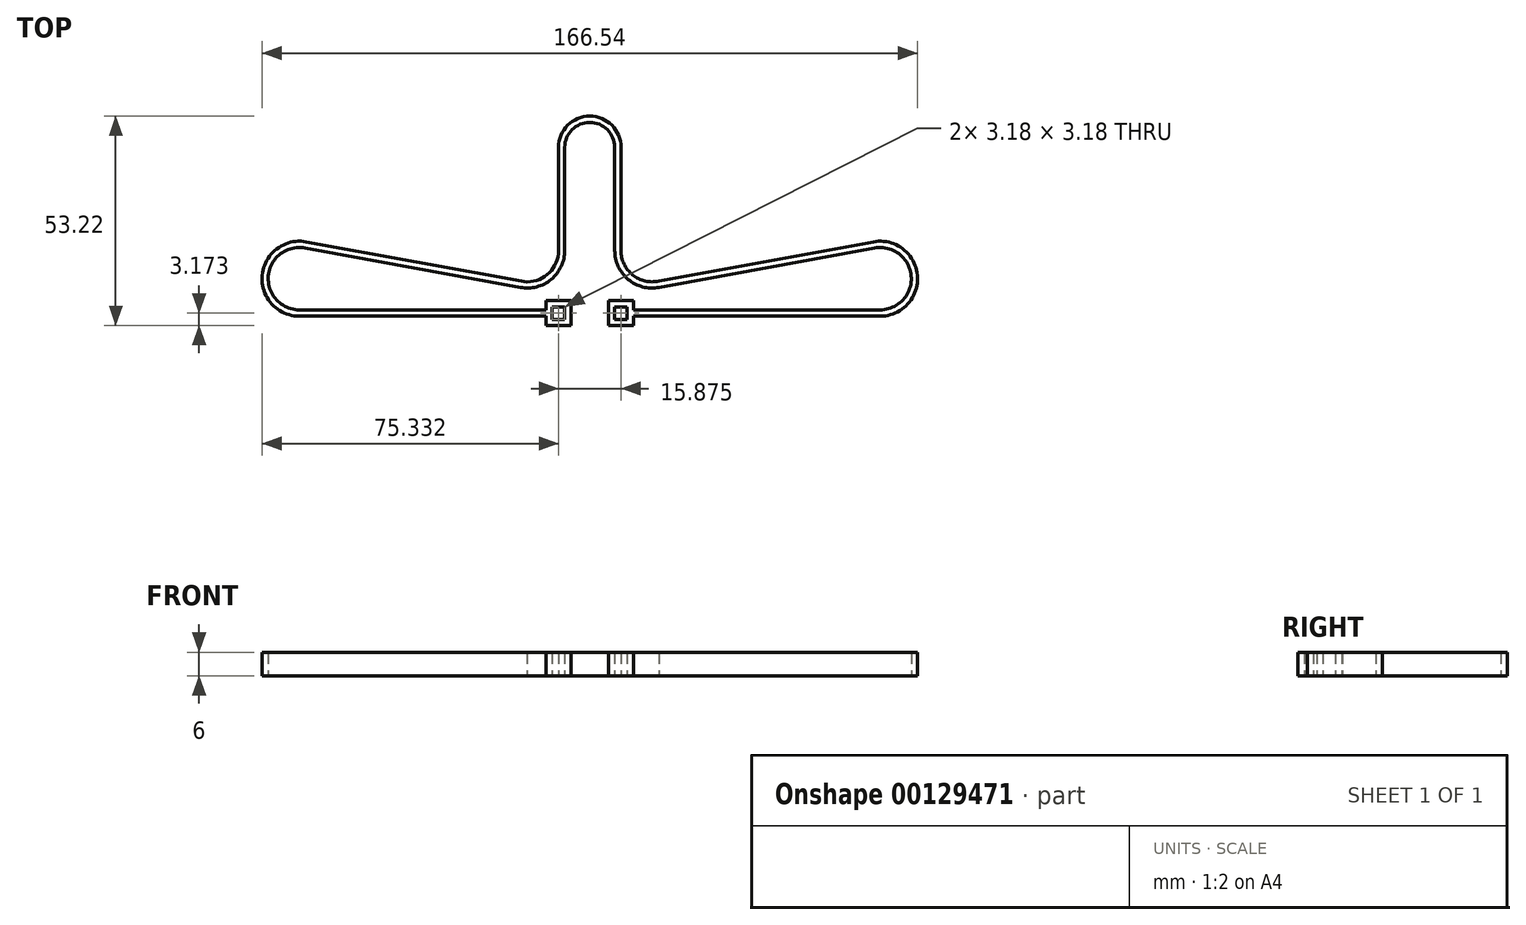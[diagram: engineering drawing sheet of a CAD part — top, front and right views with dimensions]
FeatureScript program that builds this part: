
annotation { "Feature Type Name" : "Feature", "Feature Type Description" : "" }
export const myFeature = defineFeature(function(context is Context, id is Id, definition is map)
    precondition{}
    {
        {
            var Q0;
            Q0=qCreatedBy(makeId("Top.planeOp"),FACE);
            var sketch = newSketch(context, id + "F0", { "sketchPlane" : qUnion([Q0])});
            skLineSegment(sketch, "E0", {"start": v(0, 0) * mm, "end": v(0, -26.23) * mm, "construction": true});
            skLineSegment(sketch, "E1", {"start": v(-15.88, -26.23) * mm, "end": v(15.88, -26.23) * mm, "construction": true});
            skCircle(sketch, "E2", {"center": v(0, 0) * mm, "radius": 6.35 * mm, "construction": true});
            skCircle(sketch, "E3", {"center": v(-15.88, -26.23) * mm, "radius": 7.94 * mm, "construction": true});
            skCircle(sketch, "E4", {"center": v(15.88, -26.23) * mm, "radius": 7.94 * mm, "construction": true});
            skLineSegment(sketch, "E5", {"start": v(0, -26.23) * mm, "end": v(0, -33.38) * mm, "construction": true});
            skLineSegment(sketch, "E6", {"start": v(-73.75, -33.38) * mm, "end": v(73.75, -33.38) * mm, "construction": true});
            skCircle(sketch, "E7", {"center": v(73.75, -33.38) * mm, "radius": 7.94 * mm, "construction": true});
            skCircle(sketch, "E8", {"center": v(-73.75, -33.38) * mm, "radius": 7.94 * mm, "construction": true});
            skLineSegment(sketch, "E9", {"start": v(-6.35, 0) * mm, "end": v(-6.35, -26.23) * mm});
            skLineSegment(sketch, "E10", {"start": v(-17.6, -35.6) * mm, "end": v(-72.32, -25.57) * mm});
            skLineSegment(sketch, "E11", {"start": v(6.35, -26.23) * mm, "end": v(6.35, 0) * mm});
            skArc(sketch, "E12", {"start": v(-17.6, -35.6) * mm, "mid": v(-9.78, -33.55) * mm, "end": v(-6.35, -26.23) * mm});
            skArc(sketch, "E13", {"start": v(6.35, -26.23) * mm, "mid": v(9.78, -33.55) * mm, "end": v(17.6, -35.6) * mm});
            skLineSegment(sketch, "E14", {"start": v(17.6, -35.6) * mm, "end": v(72.32, -25.57) * mm});
            skArc(sketch, "E15", {"start": v(6.35, 0) * mm, "mid": v(0, 6.35) * mm, "end": v(-6.35, 0) * mm});
            skArc(sketch, "E16", {"start": v(73.75, -41.31) * mm, "mid": v(81.65, -32.66) * mm, "end": v(72.32, -25.57) * mm});
            skArc(sketch, "E17", {"start": v(-72.32, -25.57) * mm, "mid": v(-81.65, -32.66) * mm, "end": v(-73.75, -41.31) * mm});
            skArc(sketch, "E18", {"start": v(-15.88, -34.17) * mm, "mid": v(-10.26, -31.84) * mm, "end": v(-7.94, -26.23) * mm});
            skArc(sketch, "E19", {"start": v(7.94, -26.23) * mm, "mid": v(10.9, -32.42) * mm, "end": v(17.6, -33.98) * mm});
            skLineSegment(sketch, "E20", {"start": v(-6.35, 0) * mm, "end": v(-7.94, 0) * mm, "construction": true});
            skLineSegment(sketch, "E21", {"start": v(6.35, 0) * mm, "end": v(7.94, 0) * mm, "construction": true});
            skLineSegment(sketch, "E22", {"start": v(-7.94, 0) * mm, "end": v(-7.94, -26.23) * mm});
            skLineSegment(sketch, "E23", {"start": v(7.94, 0) * mm, "end": v(7.94, -26.23) * mm});
            skArc(sketch, "E24", {"start": v(7.94, 0) * mm, "mid": v(0, 7.94) * mm, "end": v(-7.94, 0) * mm});
            skLineSegment(sketch, "E25", {"start": v(-15.88, -34.17) * mm, "end": v(-72.05, -24) * mm});
            skLineSegment(sketch, "E26", {"start": v(17.6, -33.98) * mm, "end": v(72.03, -24) * mm});
            skArc(sketch, "E27", {"start": v(73.75, -42.9) * mm, "mid": v(83.23, -32.51) * mm, "end": v(72.03, -24) * mm});
            skArc(sketch, "E28", {"start": v(-72.05, -24) * mm, "mid": v(-83.23, -32.52) * mm, "end": v(-73.75, -42.9) * mm});
            skLineSegment(sketch, "E29", {"start": v(-73.75, -41.31) * mm, "end": v(-11.11, -41.31) * mm});
            skLineSegment(sketch, "E30", {"start": v(-73.75, -42.9) * mm, "end": v(-11.11, -42.9) * mm});
            skLineSegment(sketch, "E31", {"start": v(73.75, -41.31) * mm, "end": v(11.11, -41.31) * mm});
            skLineSegment(sketch, "E32", {"start": v(73.75, -42.9) * mm, "end": v(11.11, -42.9) * mm});
            skLineSegment(sketch, "E33", {"start": v(-11.11, -42.9) * mm, "end": v(-11.11, -41.31) * mm});
            skLineSegment(sketch, "E34", {"start": v(-11.11, -41.31) * mm, "end": v(-11.11, -38.93) * mm});
            skLineSegment(sketch, "E35", {"start": v(-11.11, -38.93) * mm, "end": v(-4.76, -38.93) * mm});
            skLineSegment(sketch, "E36", {"start": v(-4.76, -38.93) * mm, "end": v(-4.76, -45.28) * mm});
            skLineSegment(sketch, "E37", {"start": v(-4.76, -45.28) * mm, "end": v(-11.11, -45.28) * mm});
            skLineSegment(sketch, "E38", {"start": v(-11.11, -45.28) * mm, "end": v(-11.11, -42.9) * mm});
            skLineSegment(sketch, "E39", {"start": v(-11.11, -42.1) * mm, "end": v(-4.76, -42.1) * mm, "construction": true});
            skLineSegment(sketch, "E40.rect.bottom", {"start": v(-6.35, -40.52) * mm, "end": v(-9.52, -40.52) * mm});
            skLineSegment(sketch, "E40.rect.top", {"start": v(-6.35, -43.7) * mm, "end": v(-9.52, -43.7) * mm});
            skLineSegment(sketch, "E40.rect.left", {"start": v(-6.35, -40.52) * mm, "end": v(-6.35, -43.7) * mm});
            skLineSegment(sketch, "E40.rect.right", {"start": v(-9.52, -40.52) * mm, "end": v(-9.52, -43.7) * mm});
            skPoint(sketch, "E40.rect.middle", {"position": v(-7.94, -42.1) * mm});
            skLineSegment(sketch, "E41", {"start": v(-9.52, -40.52) * mm, "end": v(-11.11, -40.52) * mm, "construction": true});
            skLineSegment(sketch, "E42", {"start": v(-9.52, -40.52) * mm, "end": v(-9.52, -38.93) * mm, "construction": true});
            skLineSegment(sketch, "E43", {"start": v(11.11, -42.9) * mm, "end": v(11.11, -41.31) * mm});
            skLineSegment(sketch, "E44", {"start": v(0, -33.38) * mm, "end": v(0, -42.1) * mm, "construction": true});
            skLineSegment(sketch, "E45", {"start": v(11.11, -41.31) * mm, "end": v(11.11, -38.93) * mm});
            skLineSegment(sketch, "E46", {"start": v(11.11, -38.93) * mm, "end": v(4.76, -38.93) * mm});
            skLineSegment(sketch, "E47", {"start": v(4.76, -38.93) * mm, "end": v(4.76, -45.28) * mm});
            skLineSegment(sketch, "E48", {"start": v(4.76, -45.28) * mm, "end": v(11.11, -45.28) * mm});
            skLineSegment(sketch, "E49", {"start": v(11.11, -45.28) * mm, "end": v(11.11, -42.9) * mm});
            skLineSegment(sketch, "E50", {"start": v(4.76, -42.1) * mm, "end": v(11.11, -42.1) * mm, "construction": true});
            skLineSegment(sketch, "E51.rect.bottom", {"start": v(6.35, -40.52) * mm, "end": v(9.53, -40.52) * mm});
            skLineSegment(sketch, "E51.rect.top", {"start": v(6.35, -43.7) * mm, "end": v(9.53, -43.7) * mm});
            skLineSegment(sketch, "E51.rect.left", {"start": v(6.35, -40.52) * mm, "end": v(6.35, -43.7) * mm});
            skLineSegment(sketch, "E51.rect.right", {"start": v(9.53, -40.52) * mm, "end": v(9.53, -43.7) * mm});
            skPoint(sketch, "E51.rect.middle", {"position": v(7.94, -42.1) * mm});
            skLineSegment(sketch, "E52", {"start": v(-4.76, -42.1) * mm, "end": v(4.76, -42.1) * mm, "construction": true});
            skLineSegment(sketch, "E53", {"start": v(11.11, -38.93) * mm, "end": v(15.88, -38.93) * mm, "construction": true});
            skLineSegment(sketch, "E54", {"start": v(15.88, -38.93) * mm, "end": v(15.88, -35.76) * mm, "construction": true});
            skLineSegment(sketch, "E55", {"start": v(15.88, -35.76) * mm, "end": v(15.88, -26.23) * mm, "construction": true});
            skSolve(sketch);
        }
        {
            var Q0;
            Q0=qSketchRegion(id+"F0",true);
            extrude(context, id + "F1", {"entities" : qUnion([Q0]), "depth" : 6 * mm});
        }
    });
